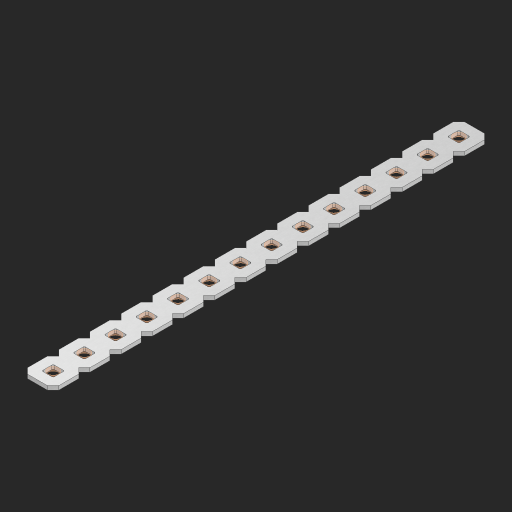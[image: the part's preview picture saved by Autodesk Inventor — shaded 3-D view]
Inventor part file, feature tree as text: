
AUTODESK INVENTOR PART (.ipt)
format: ipt  version: 2023 (Build 270158000, 158)  size: 418,816 bytes
history: native  units: in
note: dims shown in document units (in); Inventor stores cm internally (conversion verified against a paired STEP export)
features: other x15, extrude x13, sketch x2, pattern_linear x1
ambient origin geometry x8: Origin, YZ Plane, XZ Plane, XY Plane, X Axis, Y Axis, Z Axis, Center Point
bodies: Solid1 (feature_tree), Body (feature_tree)
feature tree (31):
  pattern_linear  "Rectangular Pattern1"  Spacing1=0.09in  [1 undecoded]
  sketch  "Sketch1"  dims[d1=0.5in]
  sketch  "Sketch2"  dims[d2=0.182in d3=0.09in d4=0.09in d5=0.09in d6=0.09in d7=0.09in d8=0.09in d9=0.09in d10=0.09in d11=0.02in d13=0.0in d14=0.172in d15=0.0625in d16=0.0in d19=0.5in d22=0.5in]
  other  "Srf1"
  other  "Srf126"
  other  "Srf127"
  other  "Srf128"
  other  "Srf129"
  other  "Srf130"
  other  "Srf131"
  other  "Srf250"
  other  "Srf251"
  other  "Srf252"
  other  "Srf253"
  other  "Srf254"
  other  "Srf255"
  other  "Srf256"
  other  "Circle"
  extrude  "ExtrusionSrf126"  Depth=0.09in
  extrude  "ExtrusionSrf127"  Depth=0.09in
  extrude  "ExtrusionSrf128"  Depth=0.09in
  extrude  "ExtrusionSrf129"  Depth=0.09in
  extrude  "ExtrusionSrf130"  Depth=0.09in
  extrude  "ExtrusionSrf131"  Depth=0.09in
  extrude  "ExtrusionSrf250"  Depth=0.09in
  extrude  "ExtrusionSrf251"  Depth=0.02in
  extrude  "ExtrusionSrf252"  TaperAngle=0.0deg  [1 undecoded]
  extrude  "ExtrusionSrf253"  Depth=0.5in
  extrude  "ExtrusionSrf254"  Depth=0.0625in TaperAngle=0.0deg
  extrude  "ExtrusionSrf255"  Depth=0.5in
  extrude  "ExtrusionSrf256"  Depth=0.5in
note: 2 required parameter values undecoded (feature->parameter linkage not recoverable at this tier; creation-order binding heuristic only, values carry confidence <= 0.55)
